# Revit family: DPH13PH5_WOOD
name_source: partatom
category: Generic Models
revit_build: Autodesk Revit 2015 (Build: 20140606_1530(x64)
units: mm (PartAtom-declared; Revit-internal decimal feet)

## types (1)
- BUZON_DPH13PH5_WOOD
    BIMobject category = Systems
    Brand url = http://www.buzon-world.com
    Date of publishing = 12/21/2016
    Default Elevation = 1200 mm
    Design country = Belgium
    Edition number = 1
    IFC Classification = Building Element
    Manufacturer country = Belgium
    Manufacturer name = Buzon
    Material main = Polypropylene
    Material secondary = Polypropylene
    Max Angle = 2.86°
    Min Angle = 0.00°
    NBS Reference Code = 20-20
    NBS Reference Description = Flooring And Decking Systems
    Nominal height = 0 mm  [stored 0 ft]
    Nominal width = 0 mm  [stored 0 ft]
    OmniClass Code = 23-15 17 11
    OmniClass Description = Flooring Specialties and Accessories
    Pedestal Material = Default_DPH_Material
    Product Guid = 6c906ddc-3b11-4f37-ac23-bbc59219fc5d
    Product SKU = DPH-13-PH5
    Product data url = https://bimobject.com
    Product family = DPH
    Product group = Pedestal
    Product url = http://www.buzon-world.com
    QR code = http://bimobject.com
    UNSPSC Code = 301617
    Uniclass 1.4 Code = L83121
    Uniclass 1.4 Description = Floor units
    Uniclass 2.0 Code = SS-20-20
    Uniclass 2.0 Description = Flooring And Decking Systems
    Uniclass 2015 Code = Ss_30_42_32_30
    Uniclass 2015 Name = External floor tiling systems
    Uniformat II Code = B1010
    Uniformat II Description = Floor Construction
    Weight Net (Kg) = 0

note: [stored X ft] marks values corroborated as IEEE doubles in the binary element streams (Revit-internal decimal feet)

## geometry (parser evidence)
native form markers: Sweep x38
no freeform markers — native parametric forms only
